# Revit family: RepeatingDetail_ClipIn_Knotwood_Dimensional
name_source: partatom
category: Detail Items
units: mm (PartAtom-declared; Revit-internal decimal feet)

## family parameters
Rotate with component = No
Section Shape = Not Defined
Shared = No

## types (3) — shared parameters
Manufacturer = Knotwood
ManufacturerURLProductSpecific = https://www.knotwood.com.au
URL = https://www.knotwood.com.au

## per-type parameters (varying)
| type | BattenType | Description | ManufacturerOverallDepth | ManufacturerOverallWidth | ManufacturerSpecCode | Model | ModifiedIssue |
| Batten (KECDIMBAT) | DetailItem_Batten_Knotwood_Dimensional : Batten (KECDIMBAT) | Knotwood Dimensional Cladding Batten (KECDIMBAT) | 24 mm  [stored 0.0787402 ft] | 38 mm  [stored 0.124672 ft] | KECDIMBAT | KECDIMBAT | 20231110 $ |
| Fin (KECDIMFIN) | DetailItem_Batten_Knotwood_Dimensional : Fin (KECDIMFIN) | Knotwood Dimensional Cladding Fin (KECDIMFIN) | 62 mm | 20 mm | KECDIMFIN | KECDIMFIN | 20231128 $ |
| Seam (KECDIMSEAM) | DetailItem_Batten_Knotwood_Dimensional : Seam (KECDIMSEAM) | Knotwood Dimensional Cladding Seam (KECDIMFIN) | 60 mm | 19 mm | KECDIMSEAM | KECDIMSEAM | 20231110 $ |

note: [stored X ft] marks values corroborated as IEEE doubles in the binary element streams (Revit-internal decimal feet)

## geometry (parser evidence)
native form markers: Sweep x3
no freeform markers — native parametric forms only
